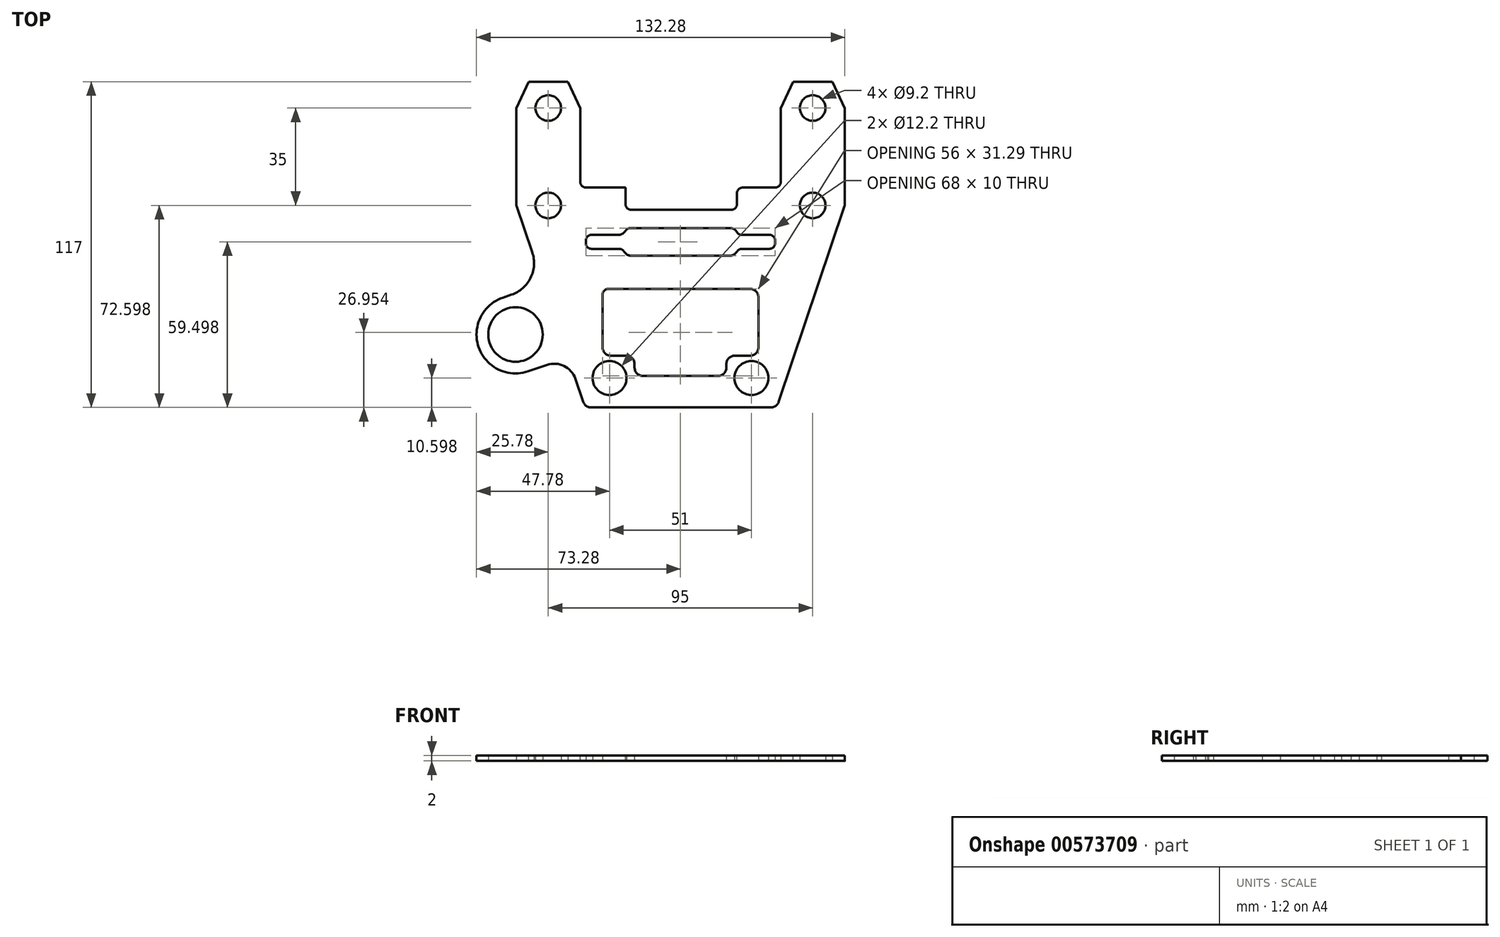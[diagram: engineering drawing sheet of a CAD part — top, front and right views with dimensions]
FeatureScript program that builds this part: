
annotation { "Feature Type Name" : "Feature", "Feature Type Description" : "" }
export const myFeature = defineFeature(function(context is Context, id is Id, definition is map)
    precondition{}
    {
        {
            var Q0;
            Q0=qCreatedBy(makeId("Top.planeOp"),FACE);
            var sketch = newSketch(context, id + "F0", { "sketchPlane" : qUnion([Q0])});
            skLineSegment(sketch, "E0.bottom", {"start": v(-36, 40.62) * mm, "end": v(36, 40.62) * mm});
            skCircle(sketch, "E1", {"center": v(-47.5, 34.22) * mm, "radius": 4.6 * mm});
            skCircle(sketch, "E2", {"center": v(47.5, 34.22) * mm, "radius": 4.6 * mm});
            skCircle(sketch, "E3", {"center": v(-25.5, -27.78) * mm, "radius": 6.1 * mm});
            skCircle(sketch, "E4", {"center": v(25.5, -27.78) * mm, "radius": 6.1 * mm});
            skLineSegment(sketch, "E5.bottom", {"start": v(-26, 4.22) * mm, "end": v(25, 4.22) * mm});
            skLineSegment(sketch, "E5.top", {"start": v(-25, -19.78) * mm, "end": v(-19.5, -19.78) * mm});
            skLineSegment(sketch, "E5.left", {"start": v(-28, 2.22) * mm, "end": v(-28, -16.78) * mm});
            skLineSegment(sketch, "E5.right", {"start": v(28, 1.22) * mm, "end": v(28, -16.78) * mm});
            skLineSegment(sketch, "E6.top", {"start": v(-13.5, -27.07) * mm, "end": v(13.5, -27.07) * mm});
            skLineSegment(sketch, "E6.left", {"start": v(-16.5, -22.78) * mm, "end": v(-16.5, -24.07) * mm});
            skLineSegment(sketch, "E6.right", {"start": v(16.5, -22.78) * mm, "end": v(16.5, -24.07) * mm});
            skPoint(sketch, "E7.visualSharp", {"position": v(-28, 4.22) * mm});
            skArc(sketch, "E7.filletArc", {"start": v(-26, 4.22) * mm, "mid": v(-27.41, 3.63) * mm, "end": v(-28, 2.22) * mm});
            skPoint(sketch, "E8.visualSharp", {"position": v(28, 4.22) * mm});
            skArc(sketch, "E8.filletArc", {"start": v(28, 1.22) * mm, "mid": v(27.12, 3.34) * mm, "end": v(25, 4.22) * mm});
            skPoint(sketch, "E9.visualSharp", {"position": v(28, -19.78) * mm});
            skArc(sketch, "E9.filletArc", {"start": v(25, -19.78) * mm, "mid": v(27.12, -18.9) * mm, "end": v(28, -16.78) * mm});
            skPoint(sketch, "E10.visualSharp", {"position": v(-28, -19.78) * mm});
            skArc(sketch, "E10.filletArc", {"start": v(-28, -16.78) * mm, "mid": v(-27.12, -18.9) * mm, "end": v(-25, -19.78) * mm});
            skArc(sketch, "E11.filletArc", {"start": v(-16.5, -24.07) * mm, "mid": v(-15.62, -26.2) * mm, "end": v(-13.5, -27.07) * mm});
            skPoint(sketch, "E12.visualSharp", {"position": v(16.5, -27.07) * mm});
            skArc(sketch, "E12.filletArc", {"start": v(13.5, -27.07) * mm, "mid": v(15.62, -26.2) * mm, "end": v(16.5, -24.07) * mm});
            skLineSegment(sketch, "E13.trimOffspring", {"start": v(19.5, -19.78) * mm, "end": v(25, -19.78) * mm});
            skPoint(sketch, "E14.visualSharp", {"position": v(-16.5, -19.78) * mm});
            skArc(sketch, "E14.filletArc", {"start": v(-16.5, -22.78) * mm, "mid": v(-17.38, -20.66) * mm, "end": v(-19.5, -19.78) * mm});
            skPoint(sketch, "E15.visualSharp", {"position": v(16.5, -19.78) * mm});
            skArc(sketch, "E15.filletArc", {"start": v(19.5, -19.78) * mm, "mid": v(17.38, -20.66) * mm, "end": v(16.5, -22.78) * mm});
            skCircle(sketch, "E16", {"center": v(0, -27.78) * mm, "radius": 45 * mm, "construction": true});
            skLineSegment(sketch, "E17", {"start": v(-34.27, -38.38) * mm, "end": v(34.59, -38.38) * mm});
            skLineSegment(sketch, "E18", {"start": v(-59, 40.62) * mm, "end": v(-59, 34.22) * mm});
            skLineSegment(sketch, "E19", {"start": v(-59, 34.22) * mm, "end": v(-52.47, 15.03) * mm});
            skLineSegment(sketch, "E20", {"start": v(59, 40.62) * mm, "end": v(59, 34.22) * mm});
            skLineSegment(sketch, "E21", {"start": v(59, 34.22) * mm, "end": v(34.59, -38.38) * mm});
            skLineSegment(sketch, "E22.bottom", {"start": v(-34, 18.62) * mm, "end": v(-20, 18.62) * mm});
            skLineSegment(sketch, "E22.top", {"start": v(-34, 23.62) * mm, "end": v(-20, 23.62) * mm});
            skLineSegment(sketch, "E22.left", {"start": v(-34, 23.62) * mm, "end": v(-34, 18.62) * mm});
            skLineSegment(sketch, "E22.right", {"start": v(34, 23.62) * mm, "end": v(34, 18.62) * mm});
            skLineSegment(sketch, "E23.bottom", {"start": v(-20, 26.12) * mm, "end": v(20, 26.12) * mm});
            skLineSegment(sketch, "E23.top", {"start": v(-20, 16.12) * mm, "end": v(20, 16.12) * mm});
            skLineSegment(sketch, "E23.left", {"start": v(-20, 26.12) * mm, "end": v(-20, 23.62) * mm});
            skLineSegment(sketch, "E23.right", {"start": v(20, 26.12) * mm, "end": v(20, 23.62) * mm});
            skLineSegment(sketch, "E24", {"start": v(-34, 21.12) * mm, "end": v(34, 21.12) * mm, "construction": true});
            skLineSegment(sketch, "E25.trimOffspring", {"start": v(-20, 18.62) * mm, "end": v(-20, 16.12) * mm});
            skLineSegment(sketch, "E26.trimOffspring", {"start": v(20, 23.62) * mm, "end": v(34, 23.62) * mm});
            skLineSegment(sketch, "E27.trimOffspring", {"start": v(20, 18.62) * mm, "end": v(34, 18.62) * mm});
            skLineSegment(sketch, "E28.trimOffspring", {"start": v(20, 18.62) * mm, "end": v(20, 16.12) * mm});
            skLineSegment(sketch, "E29.trimOffspring", {"start": v(-40.36, -20.5) * mm, "end": v(-34.27, -38.38) * mm});
            skCircle(sketch, "E30", {"center": v(-59.28, -12.16) * mm, "radius": 9.8 * mm});
            skPoint(sketch, "E30.centerSnap0", {"position": v(-39.59, -22.78) * mm});
            skCircle(sketch, "E31", {"center": v(-47.5, 69.22) * mm, "radius": 4.6 * mm});
            skCircle(sketch, "E32", {"center": v(47.5, 69.22) * mm, "radius": 4.6 * mm});
            skLineSegment(sketch, "E33", {"start": v(-59, 40.62) * mm, "end": v(-59, 78.62) * mm});
            skLineSegment(sketch, "E34", {"start": v(-59, 78.62) * mm, "end": v(-36, 78.62) * mm});
            skLineSegment(sketch, "E35", {"start": v(-36, 78.62) * mm, "end": v(-36, 40.62) * mm});
            skLineSegment(sketch, "E36", {"start": v(59, 40.62) * mm, "end": v(59, 78.62) * mm});
            skLineSegment(sketch, "E37", {"start": v(59, 78.62) * mm, "end": v(36, 78.62) * mm});
            skLineSegment(sketch, "E38", {"start": v(36, 78.62) * mm, "end": v(36, 40.62) * mm});
            skLineSegment(sketch, "E39", {"start": v(-52.47, 15.03) * mm, "end": v(-49.39, 6) * mm});
            skArc(sketch, "E40", {"start": v(-63.8, 1.1) * mm, "mid": v(-72.53, -16.67) * mm, "end": v(-54.77, -25.41) * mm});
            skPoint(sketch, "E41.endSnap0", {"position": v(-48.68, 3.93) * mm});
            skLineSegment(sketch, "E42", {"start": v(-54.77, -25.41) * mm, "end": v(-40.36, -20.5) * mm});
            skLineSegment(sketch, "E43", {"start": v(-63.8, 1.1) * mm, "end": v(-49.39, 6) * mm});
            skPoint(sketch, "E44.orphan", {"position": v(-44.9, -7.17) * mm});
            skSolve(sketch);
        }
        {
            var Q0;
            Q0 = qSketchRegion(id + "F0", true);
            extrude(context, id + "F1", {"entities" : qUnion([Q0]), "depth" : 2 * mm, "offsetDistance" : 25 * mm});
        }
        {
            var Q0;
            Q0=makeQuery(id+"F1.opExtrude","SWEPT_EDGE",EDGE,{"disambiguationData":[OSD([sQuery(id+"F0.wireOp",EDGE,"E0.bottom"),sQuery(id+"F0.wireOp",EDGE,"E18")])]});
            var Q1;
            Q1=makeQuery(id+"F1.opExtrude","SWEPT_EDGE",EDGE,{"disambiguationData":[OSD([sQuery(id+"F0.wireOp",EDGE,"E0.bottom"),sQuery(id+"F0.wireOp",EDGE,"E20")])]});
            var Q2;
            Q2=makeQuery(id+"F1.opExtrude","SWEPT_EDGE",EDGE,{"disambiguationData":[OSD([sQuery(id+"F0.wireOp",EDGE,"E20"),sQuery(id+"F0.wireOp",EDGE,"E21")])]});
            var Q3;
            Q3=makeQuery(id+"F1.opExtrude","SWEPT_EDGE",EDGE,{"disambiguationData":[OSD([sQuery(id+"F0.wireOp",EDGE,"E23.bottom"),sQuery(id+"F0.wireOp",EDGE,"E23.left")])]});
            var Q4;
            Q4=makeQuery(id+"F1.opExtrude","SWEPT_EDGE",EDGE,{"disambiguationData":[OSD([sQuery(id+"F0.wireOp",EDGE,"E23.right"),sQuery(id+"F0.wireOp",EDGE,"E26.trimOffspring")])]});
            var Q5;
            Q5=makeQuery(id+"F1.opExtrude","SWEPT_EDGE",EDGE,{"disambiguationData":[OSD([sQuery(id+"F0.wireOp",EDGE,"E22.top"),sQuery(id+"F0.wireOp",EDGE,"E22.left")])]});
            var Q6;
            Q6=makeQuery(id+"F1.opExtrude","SWEPT_EDGE",EDGE,{"disambiguationData":[OSD([sQuery(id+"F0.wireOp",EDGE,"E22.bottom"),sQuery(id+"F0.wireOp",EDGE,"E25.trimOffspring")])]});
            var Q7;
            Q7=makeQuery(id+"F1.opExtrude","SWEPT_EDGE",EDGE,{"disambiguationData":[OSD([sQuery(id+"F0.wireOp",EDGE,"E22.bottom"),sQuery(id+"F0.wireOp",EDGE,"E22.left")])]});
            var Q8;
            Q8=makeQuery(id+"F1.opExtrude","SWEPT_EDGE",EDGE,{"disambiguationData":[OSD([sQuery(id+"F0.wireOp",EDGE,"E27.trimOffspring"),sQuery(id+"F0.wireOp",EDGE,"E28.trimOffspring")])]});
            var Q9;
            Q9=makeQuery(id+"F1.opExtrude","SWEPT_EDGE",EDGE,{"disambiguationData":[OSD([sQuery(id+"F0.wireOp",EDGE,"E22.right"),sQuery(id+"F0.wireOp",EDGE,"E26.trimOffspring")])]});
            var Q10;
            Q10=makeQuery(id+"F1.opExtrude","SWEPT_EDGE",EDGE,{"disambiguationData":[OSD([sQuery(id+"F0.wireOp",EDGE,"E22.right"),sQuery(id+"F0.wireOp",EDGE,"E27.trimOffspring")])]});
            var Q11;
            Q11=makeQuery(id+"F1.opExtrude","SWEPT_EDGE",EDGE,{"disambiguationData":[OSD([sQuery(id+"F0.wireOp",EDGE,"E18"),sQuery(id+"F0.wireOp",EDGE,"E19")])]});
            fillet(context, id + "F2", {"entities" : qUnion([Q0, Q1, Q2, Q3, Q4, Q5, Q6, Q7, Q8, Q9, Q10, Q11]), "radius" : 2 * mm, "tangentPropagation" : true, "allowEdgeOverflow" : false});
        }
        {
            var Q0;
            Q0=makeQuery(id+"F1.opExtrude","SWEPT_EDGE",EDGE,{"disambiguationData":[OSD([sQuery(id+"F0.wireOp",EDGE,"E22.top"),sQuery(id+"F0.wireOp",EDGE,"E23.left")])]});
            var Q1;
            Q1=makeQuery(id+"F1.opExtrude","SWEPT_EDGE",EDGE,{"disambiguationData":[OSD([sQuery(id+"F0.wireOp",EDGE,"E23.top"),sQuery(id+"F0.wireOp",EDGE,"E25.trimOffspring")])]});
            var Q2;
            Q2=makeQuery(id+"F1.opExtrude","SWEPT_EDGE",EDGE,{"disambiguationData":[OSD([sQuery(id+"F0.wireOp",EDGE,"E23.bottom"),sQuery(id+"F0.wireOp",EDGE,"E23.right")])]});
            var Q3;
            Q3=makeQuery(id+"F1.opExtrude","SWEPT_EDGE",EDGE,{"disambiguationData":[OSD([sQuery(id+"F0.wireOp",EDGE,"E23.top"),sQuery(id+"F0.wireOp",EDGE,"E28.trimOffspring")])]});
            var Q4;
            Q4=makeQuery(id+"F1.opExtrude","SWEPT_EDGE",EDGE,{"disambiguationData":[OSD([sQuery(id+"F0.wireOp",EDGE,"E17"),sQuery(id+"F0.wireOp",EDGE,"E29.trimOffspring")])]});
            var Q5;
            Q5=makeQuery(id+"F1.opExtrude","SWEPT_EDGE",EDGE,{"disambiguationData":[OSD([sQuery(id+"F0.wireOp",EDGE,"E17"),sQuery(id+"F0.wireOp",EDGE,"E21")])]});
            fillet(context, id + "F3", {"entities" : qUnion([Q0, Q1, Q2, Q3, Q4, Q5]), "radius" : 3 * mm, "tangentPropagation" : true, "allowEdgeOverflow" : false});
        }
        {
            var Q0;
            Q0=makeQuery(id+"F1.opExtrude","CAP_FACE",FACE,{"disambiguationData":[OSD([sQuery(id+"F0.wireOp",EDGE,"E0.bottom"),sQuery(id+"F0.wireOp",EDGE,"E1"),sQuery(id+"F0.wireOp",EDGE,"E2"),sQuery(id+"F0.wireOp",EDGE,"E3"),sQuery(id+"F0.wireOp",EDGE,"E4"),sQuery(id+"F0.wireOp",EDGE,"E5.bottom"),sQuery(id+"F0.wireOp",EDGE,"E5.top"),sQuery(id+"F0.wireOp",EDGE,"E5.left"),sQuery(id+"F0.wireOp",EDGE,"E5.right"),sQuery(id+"F0.wireOp",EDGE,"E6.top"),sQuery(id+"F0.wireOp",EDGE,"E6.left"),sQuery(id+"F0.wireOp",EDGE,"E6.right"),sQuery(id+"F0.wireOp",EDGE,"E7.filletArc"),sQuery(id+"F0.wireOp",EDGE,"E8.filletArc"),sQuery(id+"F0.wireOp",EDGE,"E9.filletArc"),sQuery(id+"F0.wireOp",EDGE,"E10.filletArc"),sQuery(id+"F0.wireOp",EDGE,"E11.filletArc"),sQuery(id+"F0.wireOp",EDGE,"E12.filletArc"),sQuery(id+"F0.wireOp",EDGE,"E13.trimOffspring"),sQuery(id+"F0.wireOp",EDGE,"E14.filletArc"),sQuery(id+"F0.wireOp",EDGE,"E15.filletArc"),sQuery(id+"F0.wireOp",EDGE,"E17"),sQuery(id+"F0.wireOp",EDGE,"E18"),sQuery(id+"F0.wireOp",EDGE,"E19"),sQuery(id+"F0.wireOp",EDGE,"E20"),sQuery(id+"F0.wireOp",EDGE,"E21"),sQuery(id+"F0.wireOp",EDGE,"E22.bottom"),sQuery(id+"F0.wireOp",EDGE,"E22.top"),sQuery(id+"F0.wireOp",EDGE,"E22.left"),sQuery(id+"F0.wireOp",EDGE,"E22.right"),sQuery(id+"F0.wireOp",EDGE,"E23.bottom"),sQuery(id+"F0.wireOp",EDGE,"E23.top"),sQuery(id+"F0.wireOp",EDGE,"E23.left"),sQuery(id+"F0.wireOp",EDGE,"E23.right"),sQuery(id+"F0.wireOp",EDGE,"v7lDQAeh-jHxy-2sO5-hVS0-u2rRAW5yEIvf"),sQuery(id+"F0.wireOp",EDGE,"E25.trimOffspring"),sQuery(id+"F0.wireOp",EDGE,"E26.trimOffspring"),sQuery(id+"F0.wireOp",EDGE,"E27.trimOffspring"),sQuery(id+"F0.wireOp",EDGE,"E28.trimOffspring"),sQuery(id+"F0.wireOp",EDGE,"E29.trimOffspring")])],"isStart":false});
            var sketch = newSketch(context, id + "F4", { "sketchPlane" : qUnion([Q0])});
            skLineSegment(sketch, "E45.bottom", {"start": v(-19.73, 40.62) * mm, "end": v(20.27, 40.62) * mm});
            skLineSegment(sketch, "E45.top", {"start": v(-19.73, 32.62) * mm, "end": v(20.27, 32.62) * mm});
            skLineSegment(sketch, "E45.left", {"start": v(-19.73, 40.62) * mm, "end": v(-19.73, 32.62) * mm});
            skLineSegment(sketch, "E45.right", {"start": v(20.27, 40.62) * mm, "end": v(20.27, 32.62) * mm});
            skSolve(sketch);
        }
        {
            var Q0;
            Q0 = qSketchRegion(id + "F4", true);
            extrude(context, id + "F5", {"entities" : qUnion([Q0]), "operationType" : NewBodyOperationType.REMOVE, "oppositeDirection" : true, "depth" : 25 * mm, "offsetDistance" : 25 * mm});
        }
        {
            var Q0;
            Q0=makeQuery(id+"F5.boolean.opBoolean","COPY",EDGE,{"derivedFrom":makeQuery(id+"F5.opExtrude","SWEPT_EDGE",EDGE,{"disambiguationData":[OSD([sQuery(id+"F0.wireOp",EDGE,"E0.bottom"),sQuery(id+"F4.wireOp",EDGE,"E45.bottom"),sQuery(id+"F4.wireOp",EDGE,"E45.left")])]})});
            var Q1;
            Q1=makeQuery(id+"F5.boolean.opBoolean","COPY",EDGE,{"derivedFrom":makeQuery(id+"F5.opExtrude","SWEPT_EDGE",EDGE,{"disambiguationData":[OSD([sQuery(id+"F4.wireOp",EDGE,"E45.top"),sQuery(id+"F4.wireOp",EDGE,"E45.left")])]})});
            var Q2;
            Q2=makeQuery(id+"F5.boolean.opBoolean","COPY",EDGE,{"derivedFrom":makeQuery(id+"F5.opExtrude","SWEPT_EDGE",EDGE,{"disambiguationData":[OSD([sQuery(id+"F0.wireOp",EDGE,"E0.bottom"),sQuery(id+"F4.wireOp",EDGE,"E45.bottom"),sQuery(id+"F4.wireOp",EDGE,"E45.right")])]})});
            var Q3;
            Q3=makeQuery(id+"F5.boolean.opBoolean","COPY",EDGE,{"derivedFrom":makeQuery(id+"F5.opExtrude","SWEPT_EDGE",EDGE,{"disambiguationData":[OSD([sQuery(id+"F4.wireOp",EDGE,"E45.top"),sQuery(id+"F4.wireOp",EDGE,"E45.right")])]})});
            fillet(context, id + "F6", {"entities" : qUnion([Q0, Q1, Q2, Q3]), "radius" : 2 * mm, "tangentPropagation" : true, "allowEdgeOverflow" : false});
        }
        {
            var Q0;
            Q0=makeQuery(id+"F1.opExtrude","SWEPT_EDGE",EDGE,{"disambiguationData":[OSD([sQuery(id+"F0.wireOp",EDGE,"E19"),sQuery(id+"F0.wireOp",EDGE,"v7lDQAeh-jHxy-2sO5-hVS0-u2rRAW5yEIvf")])]});
            var Q1;
            Q1=makeQuery(id+"F1.opExtrude","SWEPT_EDGE",EDGE,{"disambiguationData":[OSD([sQuery(id+"F0.wireOp",EDGE,"v7lDQAeh-jHxy-2sO5-hVS0-u2rRAW5yEIvf"),sQuery(id+"F0.wireOp",EDGE,"E29.trimOffspring")])]});
            fillet(context, id + "F7", {"entities" : qUnion([Q0, Q1]), "radius" : 8 * mm, "tangentPropagation" : true, "allowEdgeOverflow" : false});
        }
        {
            var Q0;
            Q0=makeQuery(id+"F1.opExtrude","SWEPT_EDGE",EDGE,{"disambiguationData":[OSD([sQuery(id+"F0.wireOp",EDGE,"E39"),sQuery(id+"F0.wireOp",EDGE,"E43")])]});
            fillet(context, id + "F8", {"entities" : qUnion([Q0]), "radius" : 12 * mm, "tangentPropagation" : true, "allowEdgeOverflow" : false});
        }
        {
            var Q0;
            Q0=makeQuery(id+"F1.opExtrude","SWEPT_EDGE",EDGE,{"disambiguationData":[OSD([sQuery(id+"F0.wireOp",EDGE,"E33"),sQuery(id+"F0.wireOp",EDGE,"E34")])]});
            var Q1;
            Q1=makeQuery(id+"F1.opExtrude","SWEPT_EDGE",EDGE,{"disambiguationData":[OSD([sQuery(id+"F0.wireOp",EDGE,"E34"),sQuery(id+"F0.wireOp",EDGE,"E35")])]});
            var Q2;
            Q2=makeQuery(id+"F1.opExtrude","SWEPT_EDGE",EDGE,{"disambiguationData":[OSD([sQuery(id+"F0.wireOp",EDGE,"E37"),sQuery(id+"F0.wireOp",EDGE,"E38")])]});
            chamfer(context, id + "F9", {"entities" : qUnion([Q0, Q1, Q2]), "chamferType" : ChamferType.TWO_OFFSETS, "width1" : 9.5 * mm, "oppositeDirection" : false, "width2" : 4.5 * mm, "tangentPropagation" : true});
        }
        {
            var Q0;
            Q0=makeQuery(id+"F1.opExtrude","SWEPT_EDGE",EDGE,{"disambiguationData":[OSD([sQuery(id+"F0.wireOp",EDGE,"E36"),sQuery(id+"F0.wireOp",EDGE,"E37")])]});
            chamfer(context, id + "F10", {"entities" : qUnion([Q0]), "chamferType" : ChamferType.TWO_OFFSETS, "width1" : 4.5 * mm, "oppositeDirection" : false, "width2" : 9.5 * mm, "tangentPropagation" : true});
        }
    });
